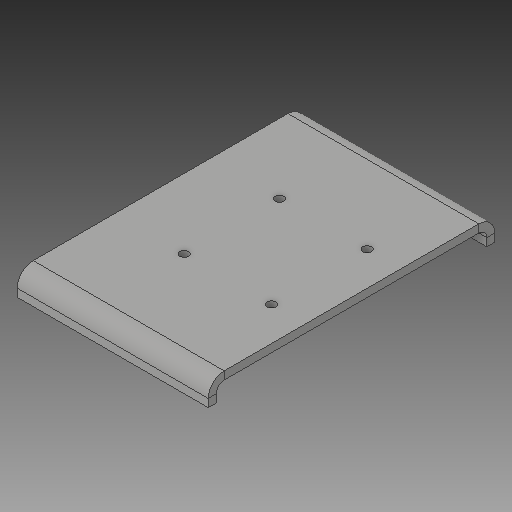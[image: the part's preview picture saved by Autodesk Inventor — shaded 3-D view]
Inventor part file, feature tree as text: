
AUTODESK INVENTOR PART (.ipt)
format: ipt  version: 2019 (Build 230136000, 136)  size: 143,360 bytes
history: native  units: mm
features: sheet_metal_op x4, other x4, reference x4, sketch x3, extrude x1
ambient origin geometry x8: Origin, YZ Plane, XZ Plane, XY Plane, X Axis, Y Axis, Z Axis, Center Point
bodies: Solid1 (feature_tree)
feature tree (16):
  sheet_metal_op  "Face1"
  sheet_metal_op  "Flange1"
  extrude  "Extrusion1"  Depth=15.0mm
  sketch  "Sketch1"  dims[d0=180.0mm d1=15.0mm]
  other  "Plate1"
  sketch  "Sketch2"  dims[d2=120.0mm]
  other  "Plate2"
  sheet_metal_op  "Bend1"
  sheet_metal_op  "Corner1"
  sketch  "Sketch3"  dims[d3=5.0mm d4=5.0mm d5=2.5mm d6=10.0mm d7=5.0mm d8=15.0mm d9=90.0deg d10=5.0mm d11=20.0mm d12=5.0mm d13=5.0mm d14=10.0mm d15=0.0mm]
  reference  "Reference1"
  reference  "Reference2"
  reference  "Reference3"
  reference  "Reference4"
  parser-record x1  (decoder bookkeeping rows leaked as tree rows — omitted from the tree; the rows remain in map.json)
  other  "zplate_assembly.iam"
note: 1 file-system path scrubbed to <path> (originals preserved in map.json)
